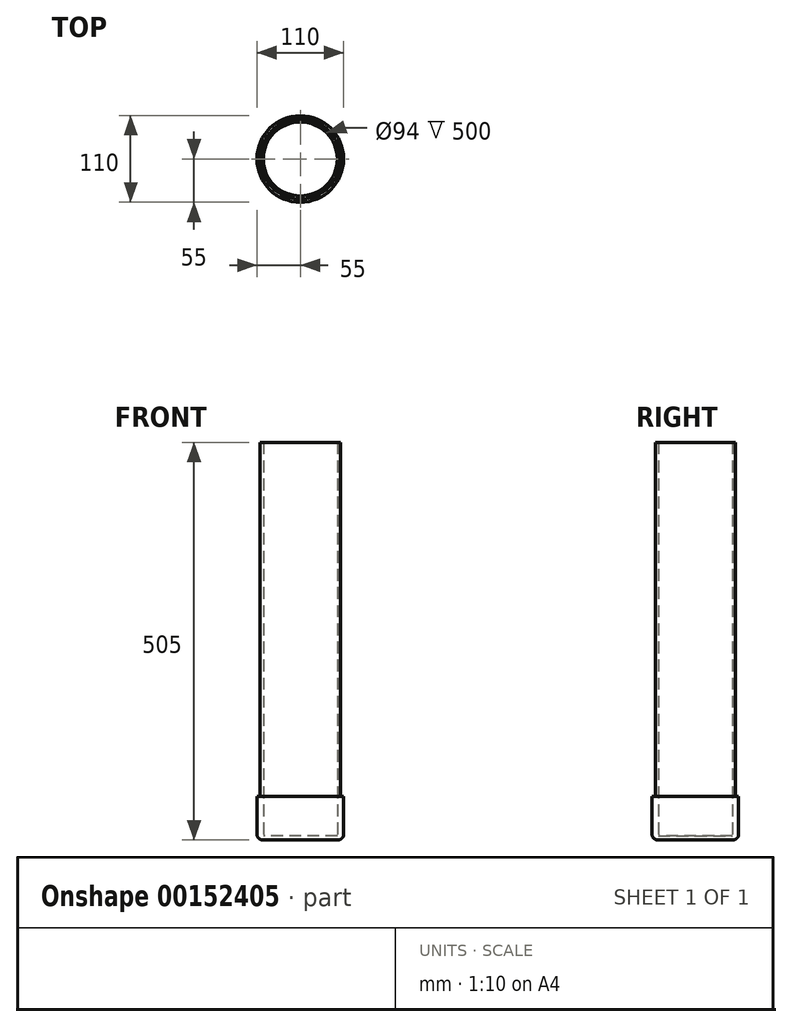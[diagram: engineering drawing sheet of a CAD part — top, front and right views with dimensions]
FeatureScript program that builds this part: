
annotation { "Feature Type Name" : "Feature", "Feature Type Description" : "" }
export const myFeature = defineFeature(function(context is Context, id is Id, definition is map)
    precondition{}
    {
        {
            var Q0;
            Q0=qCreatedBy(makeId("Top.planeOp"),FACE);
            var sketch = newSketch(context, id + "F0", { "sketchPlane" : qUnion([Q0])});
            skCircle(sketch, "E0", {"center": v(0, 0) * mm, "radius": 55 * mm});
            skCircle(sketch, "E1", {"center": v(0, 0) * mm, "radius": 51 * mm});
            skCircle(sketch, "E2", {"center": v(0, 0) * mm, "radius": 47 * mm});
            skSolve(sketch);
        }
        {
            var Q0;
            Q0=qSketchRegion(id+"F0",true);
            var Q1;
            Q1=makeQuery(id+"F0.imprint","IMPRINT",FACE,{"disambiguationData":[TD([[makeQuery(id+"F0.imprint","IMPRINT",EDGE,{"derivedFrom":sQuery(id+"F0.wireOp",EDGE,"E1")}),1.0]])]});
            var Q2;
            Q2=makeQuery(id+"F0.imprint","IMPRINT",FACE,{"disambiguationData":[TD([[makeQuery(id+"F0.imprint","IMPRINT",EDGE,{"derivedFrom":sQuery(id+"F0.wireOp",EDGE,"E2")}),1.0]])]});
            extrude(context, id + "F1", {"entities" : qUnion([Q0, Q1, Q2]), "oppositeDirection" : true, "depth" : 5 * mm});
        }
        {
            var Q0;
            Q0=makeQuery(id+"F0.imprint","IMPRINT",FACE,{"disambiguationData":[TD([[makeQuery(id+"F0.imprint","IMPRINT",EDGE,{"derivedFrom":sQuery(id+"F0.wireOp",EDGE,"E1")}),1.0]])]});
            extrude(context, id + "F2", {"entities" : qUnion([Q0]), "operationType" : NewBodyOperationType.ADD, "depth" : 500 * mm});
        }
        {
            var Q0;
            Q0=makeQuery(id+"F0.imprint","IMPRINT",FACE,{"disambiguationData":[TD([[makeQuery(id+"F0.imprint","IMPRINT",EDGE,{"derivedFrom":sQuery(id+"F0.wireOp",EDGE,"E0")}),1.0]])]});
            extrude(context, id + "F3", {"entities" : qUnion([Q0]), "operationType" : NewBodyOperationType.ADD, "depth" : 50 * mm});
        }
        {
            var Q0;
            Q0=makeQuery(id+"F1.opExtrude","CAP_EDGE",EDGE,{"disambiguationData":[OSD([sQuery(id+"F0.wireOp",EDGE,"E0")])],"isStart":false});
            fillet(context, id + "F4", {"entities" : qUnion([Q0]), "radius" : 7 * mm, "tangentPropagation" : true, "allowEdgeOverflow" : false});
        }
    });
